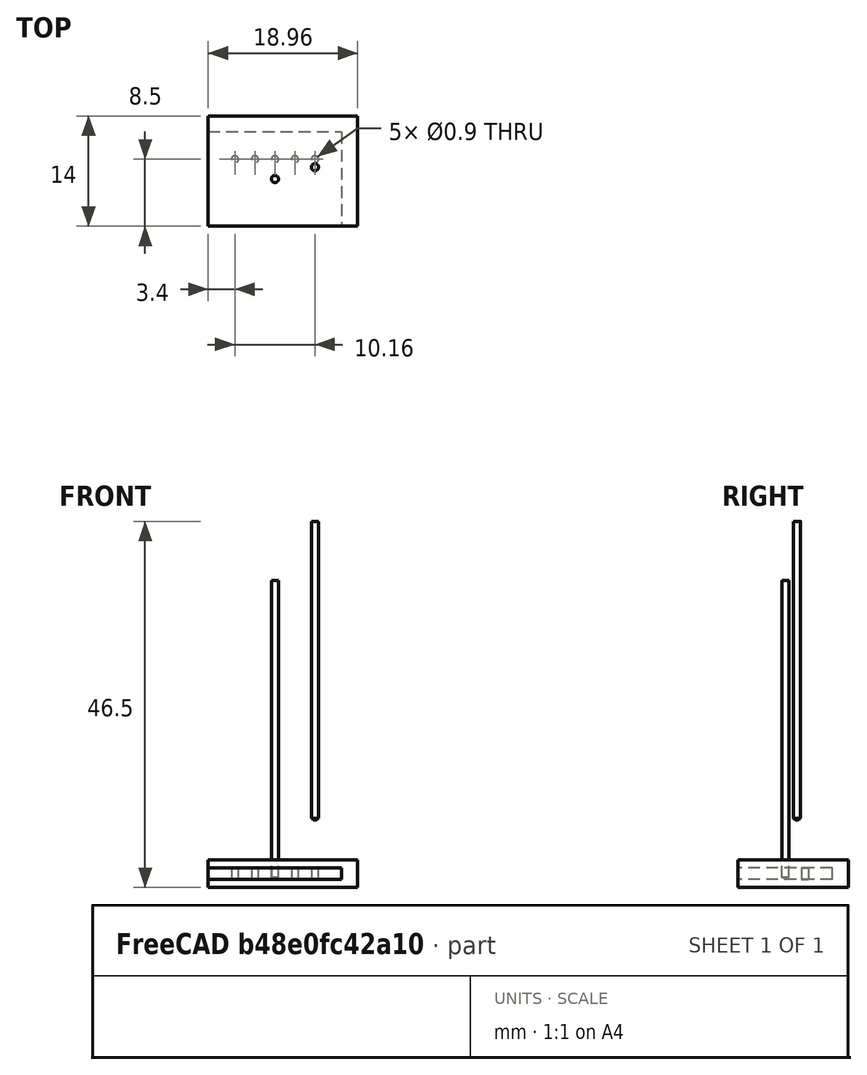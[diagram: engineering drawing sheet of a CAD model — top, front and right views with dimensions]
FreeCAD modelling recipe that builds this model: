
FCSTD DOCUMENT  (FreeCAD 0.20R29177 (Git))
Label: PCB connector drilling gaps
License: All rights reserved
LicenseURL: http://en.wikipedia.org/wiki/All_rights_reserved
objects: Part::FeaturePython×4, App::DocumentObjectGroup×3, Path::FeaturePython×3, Sketcher::SketchObject×1, PartDesign::Pad×1, PartDesign::Body×1, Mesh::FeaturePython×1, App::FeaturePython×1
note: 8 computed .brp shape members not serialized (recipe doc carries the construction recipe); baked Part::Feature solids carry a one-line shape summary decoded from their .brp

FEATURE [Sketcher::SketchObject] Sketch
  FullyConstrained = true
  MapMode = 5
  Support = -> [XY_Plane]
  sketch-geometry (15):
    g0: LineSegment StartX=-8.48 StartY=6 StartZ=0 EndX=8.48 EndY=6 EndZ=0
    g1: LineSegment StartX=8.48 StartY=6 StartZ=0 EndX=8.48 EndY=-6 EndZ=0
    g2: LineSegment StartX=8.48 StartY=-6 StartZ=0 EndX=-8.48 EndY=-6 EndZ=0
    g3: LineSegment StartX=-8.48 StartY=-6 StartZ=0 EndX=-8.48 EndY=6 EndZ=0
    g4: LineSegment StartX=-8.48 StartY=2.5 StartZ=0 EndX=8.48 EndY=2.5 EndZ=0
    g5: LineSegment StartX=5.08 StartY=6 StartZ=0 EndX=5.08 EndY=-6 EndZ=0
    g6: LineSegment StartX=2.54 StartY=6 StartZ=0 EndX=2.54 EndY=-6 EndZ=0
    g7: LineSegment StartX=2e-15 StartY=-6 StartZ=0 EndX=2e-15 EndY=6 EndZ=0
    g8: LineSegment StartX=-2.54 StartY=6 StartZ=0 EndX=-2.54 EndY=-6 EndZ=0
    g9: LineSegment StartX=-5.08 StartY=-6 StartZ=0 EndX=-5.08 EndY=6 EndZ=0
    g10: Circle CenterX=-5.08 CenterY=2.5 CenterZ=0 NormalX=0 NormalY=0 NormalZ=1 AngleXU=0 Radius=0.45
    g11: Circle CenterX=-2.54 CenterY=2.5 CenterZ=0 NormalX=0 NormalY=0 NormalZ=1 AngleXU=0 Radius=0.45
    g12: Circle CenterX=2e-15 CenterY=2.5 CenterZ=0 NormalX=0 NormalY=0 NormalZ=1 AngleXU=0 Radius=0.45
    g13: Circle CenterX=2.54 CenterY=2.5 CenterZ=0 NormalX=0 NormalY=0 NormalZ=1 AngleXU=0 Radius=0.45
    g14: Circle CenterX=5.08 CenterY=2.5 CenterZ=0 NormalX=0 NormalY=0 NormalZ=1 AngleXU=0 Radius=0.45
  constraints (47):
    c: Coincident(g0,g1)
    c: Coincident(g1,g2)
    c: Coincident(g2,g3)
    c: Coincident(g3,g0)
    c: Horizontal(g0)
    c: Horizontal(g2)
    c: Vertical(g1)
    c: Vertical(g3)
    c: Symmetric(g0,g1,g-1)
    c: DistanceY(g3,g3) = 12
    c: DistanceX(g0,g0) = 16.96
    c: PointOnObject(g4,g3)
    c: PointOnObject(g4,g1)
    c: Horizontal(g4)
    c: PointOnObject(g5,g0)
    c: PointOnObject(g5,g2)
    c: Vertical(g5)
    c: Distance(g5,g0) = 3.4
    c: Distance(g4,g1) = 8.5
    c: PointOnObject(g6,g0)
    c: PointOnObject(g6,g2)
    c: Vertical(g6)
    c: PointOnObject(g7,g2)
    c: PointOnObject(g7,g0)
    c: Vertical(g7)
    c: PointOnObject(g8,g0)
    c: PointOnObject(g8,g2)
    c: Vertical(g8)
    c: PointOnObject(g9,g2)
    c: PointOnObject(g9,g0)
    c: Vertical(g9)
    c: Distance(g6,g5) = 2.54
    c: Distance(g6,g7) = 2.54
    c: Distance(g7,g8) = 2.54
    c: Distance(g8,g9) = 2.54
    c: PointOnObject(g10,g9)
    c: PointOnObject(g11,g4)
    c: PointOnObject(g12,g7)
    c: PointOnObject(g13,g4)
    c: PointOnObject(g14,g4)
    c: Equal(g10, g11-g14) x4
    c: Diameter(g10) = 0.9
    c: PointOnObject(g10,g4)
    c: PointOnObject(g11,g8)
    c: PointOnObject(g12,g4)
    c: PointOnObject(g13,g6)
    c: PointOnObject(g14,g5)
FEATURE [PartDesign::Pad] Pad
  Direction = (0,0,1)
  Length = 1.5
  Length2 = 10
  Profile = -> Sketch
  ReferenceAxis = -> Sketch [N_Axis]
  Refine = true
  Type = 0
FEATURE [PartDesign::Body] Body
  Group = -> [Sketch,Pad]
  Origin = -> Origin
  Tip = -> Pad
FEATURE [Mesh::FeaturePython] CutMaterial  # WARN: FeaturePython — macro-defined, semantics opaque (R4)
FEATURE [Part::FeaturePython] CutTool  # WARN: FeaturePython — macro-defined, semantics opaque (R4)
  Placement = pos=(5.08,1.5,7.5) rot=(0,0,1;0rad)
FEATURE [Part::FeaturePython] Clone  label="Model-Body"  # Draft clone (typed FeaturePython)
  AttacherType = Attacher::AttachEngine3D
  Fuse = false
  Objects = -> [Body]
  PathResource = Model
  Scale = (1,1,1)
FEATURE [App::DocumentObjectGroup] Model
  Group = -> [Clone]
FEATURE [Part::FeaturePython] Stock  # WARN: FeaturePython — macro-defined, semantics opaque (R4)
  Base = -> Model
  ExtXneg = 1
  ExtXpos = 1
  ExtYneg = 1
  ExtYpos = 1
  ExtZneg = 1
  ExtZpos = 1
  Placement = pos=(-7.48,-5,0) rot=(0,0,1;0rad)
  StockType = FromBase
FEATURE [Part::FeaturePython] ToolBit001  label="0.9mm_Drill"  # Path/CAM toolbit (typed FeaturePython)
  BitPropertyNames = Chipload | Diameter | Flutes | Length | Material | TipAngle
  BitShape = C:/Program Files/FreeCAD 0.20/Mod\Path\Tools\Shape\drill.fcstd
  Chipload = 0
  Diameter = 0.9
  File = <userpath>/AppData/Roaming/FreeCAD/Macro/Bit/0.9mm_Drill.fctb
  Flutes = 0
  Length = 38
  Material = 0
  ShapeName = drill
  TipAngle = 119
FEATURE [Path::FeaturePython] __9mm_Drill  label="0.9mm_Drill001"  # Path/CAM operation (typed FeaturePython)
  HorizFeed = 0
  HorizRapid = 0
  SpindleDir = 0
  SpindleSpeed = 0
  Tool = -> ToolBit001
  ToolNumber = 2
  VertFeed = 0
  VertRapid = 0
  expr: HorizRapid = SetupSheet.HorizRapid
  expr: VertRapid = SetupSheet.VertRapid
FEATURE [App::DocumentObjectGroup] Tools
  Group = -> [__9mm_Drill]
FEATURE [App::FeaturePython] SetupSheet  # Path/CAM operation (typed FeaturePython)
  ClearanceHeightExpression = OpStockZMax+SetupSheet.ClearanceHeightOffset
  ClearanceHeightOffset = 5
  CoolantMode = 0
  CoolantModes = None | Flood | Mist
  FinalDepthExpression = OpFinalDepth
  HorizRapid = 0
  SafeHeightExpression = OpStockZMax+SetupSheet.SafeHeightOffset
  SafeHeightOffset = 3
  StartDepthExpression = OpStartDepth
  StepDownExpression = OpToolDiameter
  VertRapid = 0
FEATURE [Path::FeaturePython] Drilling  # Path/CAM operation (typed FeaturePython)
  Active = true
  AddTipLength = false
  Base = -> [Clone]
  ClearanceHeight = 7.5
  CoolantMode = 0
  CycleTime = Cycletime Error
  DwellEnabled = false
  DwellTime = 1
  ExtraOffset = 0
  FinalDepth = -3
  OpFinalDepth = 0
  OpStartDepth = 2.5
  OpStockZMax = 2.5
  OpStockZMin = -1
  OpToolDiameter = 0.9
  PeckDepth = 0.675
  PeckEnabled = false
  RetractHeight = 5.5
  ReturnLevel = 0
  SafeHeight = 5.5
  StartDepth = 2.5
  ToolController = -> __9mm_Drill
  expr: ClearanceHeight = OpStockZMax + SetupSheet.ClearanceHeightOffset
  expr: FinalDepth = -3
  expr: PeckDepth = OpToolDiameter * 0.75
  expr: RetractHeight = StartDepth + SetupSheet.SafeHeightOffset
  expr: SafeHeight = OpStockZMax + SetupSheet.SafeHeightOffset
  expr: StartDepth = OpStartDepth
FEATURE [App::DocumentObjectGroup] Operations
  Group = -> [Drilling]
FEATURE [Path::FeaturePython] Job  # Path/CAM operation (typed FeaturePython)
  CycleTime = 00:00:00
  Fixtures = G54
  GeometryTolerance = 0.01
  JobType = 0
  LastPostProcessDate = 2022-09-04 13:50:18.449446
  LastPostProcessOutput = <userpath>/OneDrive/02 Arduino/01_Projects/ESP32_Radiator_ventilator/Drill PCB holes.gcode
  Model = -> Model
  Operations = -> Operations
  OrderOutputBy = 0
  PostProcessor = 8
  PostProcessorArgs = --translate_drill
  SetupSheet = -> SetupSheet
  SplitOutput = false
  Stock = -> Stock
  Tools = -> Tools
